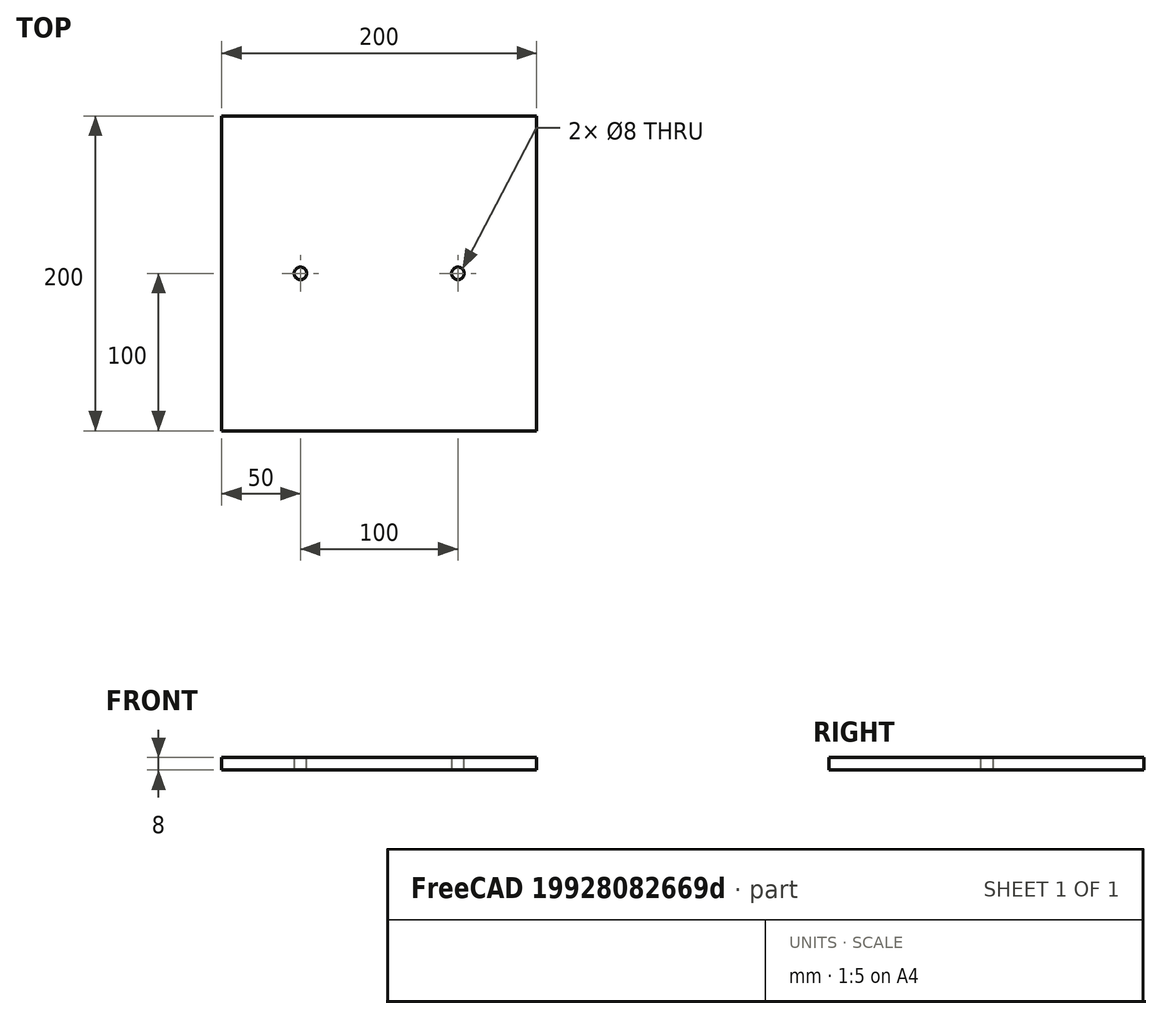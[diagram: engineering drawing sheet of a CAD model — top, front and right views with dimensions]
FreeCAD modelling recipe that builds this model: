
FCSTD DOCUMENT  (FreeCAD 1.0R39285 (Git))
Label: Supporting-Plate
License: All rights reserved
objects: Sketcher::SketchObject×1, PartDesign::Pad×1, PartDesign::Body×1
note: 6 computed .brp shape members not serialized (recipe doc carries the construction recipe); baked Part::Feature solids carry a one-line shape summary decoded from their .brp

FEATURE [Sketcher::SketchObject] Sketch
  ArcFitTolerance = 1e-06
  AttachmentSupport = -> [XY_Plane]
  FullyConstrained = true
  MakeInternals = false
  MapMode = 5
  sketch-geometry (10):
    g0: LineSegment [constr] StartX=0 StartY=0 StartZ=0 EndX=50 EndY=0 EndZ=0
    g1: LineSegment [constr] StartX=0 StartY=0 StartZ=0 EndX=-50 EndY=0 EndZ=0
    g2: Circle CenterX=-50 CenterY=0 CenterZ=0 NormalX=0 NormalY=0 NormalZ=1 AngleXU=0 Radius=4
    g3: Circle CenterX=50 CenterY=0 CenterZ=0 NormalX=0 NormalY=0 NormalZ=1 AngleXU=0 Radius=4
    g4: LineSegment [constr] StartX=0 StartY=0 StartZ=0 EndX=0 EndY=100 EndZ=0
    g5: LineSegment StartX=0 StartY=100 StartZ=0 EndX=100 EndY=100 EndZ=0
    g6: LineSegment StartX=100 StartY=100 StartZ=0 EndX=100 EndY=-100 EndZ=0
    g7: LineSegment StartX=100 StartY=-100 StartZ=0 EndX=-100 EndY=-100 EndZ=0
    g8: LineSegment StartX=-100 StartY=-100 StartZ=0 EndX=-100 EndY=100 EndZ=0
    g9: LineSegment StartX=-100 StartY=100 StartZ=0 EndX=0 EndY=100 EndZ=0
  constraints (27):
    c: Distance(g0) = 50
    c: Coincident(g0,g-1)
    c: PointOnObject(g0,g-1)
    c: Distance(g1) = 50
    c: Coincident(g1,g0)
    c: PointOnObject(g1,g-1)
    c: Diameter(g2) = 8
    c: Coincident(g2,g1)
    c: Diameter(g3) = 8
    c: Coincident(g3,g0)
    c: Distance(g4) = 100
    c: Coincident(g4,g0)
    c: PointOnObject(g4,g-2)
    c: Distance(g5) = 100
    c: Coincident(g5,g4)
    c: Horizontal(g5)
    c: Distance(g6) = 200
    c: Coincident(g6,g5)
    c: Vertical(g6)
    c: Distance(g7) = 200
    c: Coincident(g7,g6)
    c: Horizontal(g7)
    c: Distance(g8) = 200
    c: Coincident(g8,g7)
    c: Vertical(g8)
    c: Coincident(g9,g8)
    c: Coincident(g9,g4)
FEATURE [PartDesign::Pad] Pad
  Direction = (0,0,1)
  Length = 8
  Length2 = 10
  Profile = -> Sketch
  ReferenceAxis = -> Sketch [N_Axis]
  Refine = true
  Suppressed = false
  Type = 0
FEATURE [PartDesign::Body] Body
  AllowCompound = false
  Group = -> [Sketch,Pad]
  Origin = -> Origin
  Tip = -> Pad
